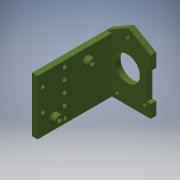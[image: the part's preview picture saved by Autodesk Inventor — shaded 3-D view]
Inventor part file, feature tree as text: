
AUTODESK INVENTOR PART (.ipt)
format: ipt  version: 2018 (Build 220112000, 112)  size: 222,720 bytes
history: native  units: in
note: dims shown in document units (in); Inventor stores cm internally (conversion verified against a paired STEP export)
features: extrude x9, sketch x7, projected_geometry x2, plane x1
ambient origin geometry x8: Origin, YZ Plane, XZ Plane, XY Plane, X Axis, Y Axis, Z Axis, Center Point
bodies: Solid1 (feature_tree)
feature tree (19):
  sketch  "Sketch1"  dims[d0=0.385in d1=0.385in]
  extrude  "Extrusion1"  Depth=0.385in
  extrude  "Extrusion2"  Depth=0.5in
  extrude  "Extrusion3"  Depth=0.5in
  extrude  "Extrusion4"  Depth=0.25in TaperAngle=0.0deg
  extrude  "Extrusion5"  Depth=0.5in
  extrude  "Extrusion7"  Depth=2.0in
  plane  "Work Plane1"
  extrude  "Extrusion12"  Depth=0.25in
  extrude  "Extrusion13"  Depth=0.25in
  extrude  "Extrusion14"  Depth=0.25in
  sketch  "Sketch2"  dims[d4=2.08in d5=0.5in]
  sketch  "Sketch3"  dims[d6=0.75in d7=0.5in]
  projected_geometry  "Projected Loop1"
  sketch  "Sketch5"  dims[d8=1.125in d9=0.25in d10=0.0in]
  sketch  "Sketch10"  dims[d11=0.5in d12=0.0in d13=0.1935in]
  sketch  "Sketch11"  dims[d14=0.5in d15=0.0in d16=2.0in]
  sketch  "Sketch12"  dims[d17=0.25in d18=0.0in d19=0.768in d20=0.699in d22=1.122in d23=2.5in d24=0.0in d25=0.25in d26=2.0in d27=0.25in d33=0.1935in d38=1.0in d39=0.0in d46=1.25in d47=1.25in d48=1.25in d49=1.25in d50=2.375in d51=1.0in d58=1.25in d77=0.1935in d78=0.25in d79=0.25in d80=1.9685in d82=0.5in d83=0.3937in d85=1.0in d87=1.0in d88=0.0in d89=30.0deg d90=30.0deg d91=1.4348in d92=0.02in d93=1.0in d94=0.0in d95=0.185in d96=0.185in d97=0.5in d98=0.5in d99=0.25in d100=1.0in d101=0.0in]
  projected_geometry  "Projected Loop2"
